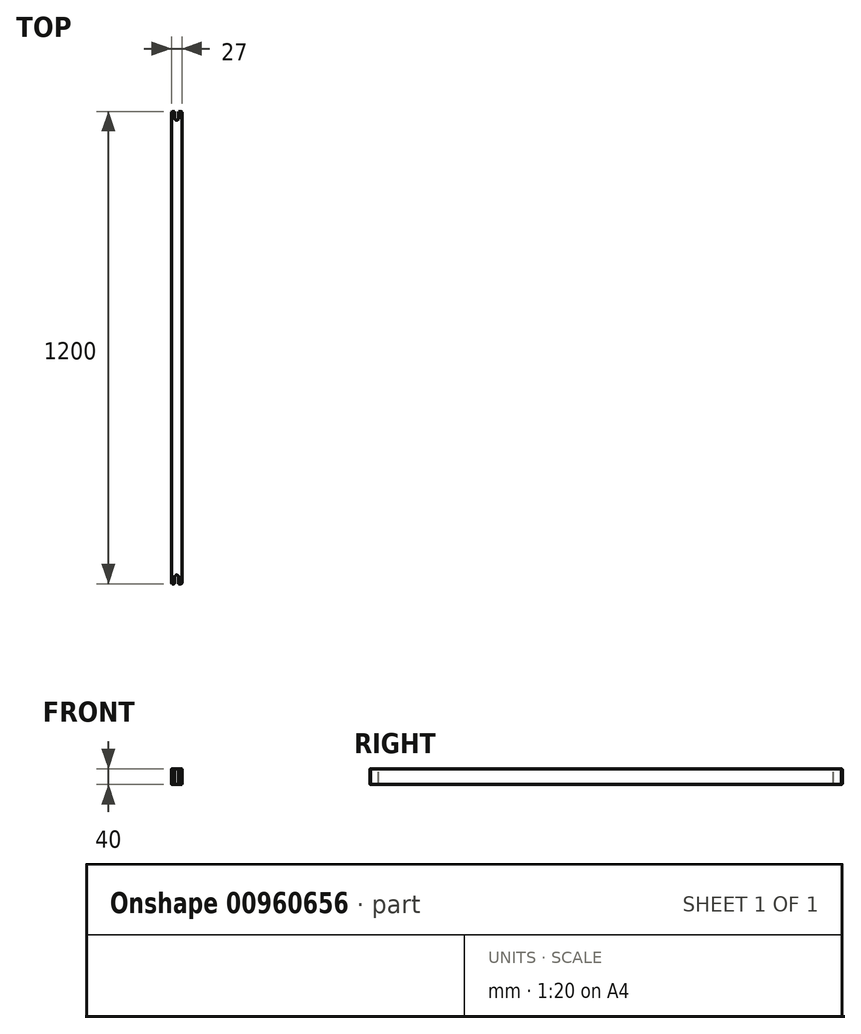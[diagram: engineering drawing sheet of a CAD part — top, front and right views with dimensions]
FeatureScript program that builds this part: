
annotation { "Feature Type Name" : "Feature", "Feature Type Description" : "" }
export const myFeature = defineFeature(function(context is Context, id is Id, definition is map)
    precondition{}
    {
        {
            var Q0;
            Q0=qCreatedBy(makeId("Front.planeOp"),FACE);
            var sketch = newSketch(context, id + "F0", { "sketchPlane" : qUnion([Q0])});
            skLineSegment(sketch, "E0.bottom", {"start": v(0, 0) * mm, "end": v(27, 0) * mm});
            skLineSegment(sketch, "E0.top", {"start": v(0, 40) * mm, "end": v(27, 40) * mm});
            skLineSegment(sketch, "E0.left", {"start": v(0, 0) * mm, "end": v(0, 40) * mm});
            skLineSegment(sketch, "E0.right", {"start": v(27, 0) * mm, "end": v(27, 40) * mm});
            skSolve(sketch);
        }
        {
            var Q0;
            Q0=makeQuery(id+"F0.imprint","IMPRINT",FACE,{"disambiguationData":[TD([[makeQuery(id+"F0.imprint","IMPRINT",EDGE,{"derivedFrom":sQuery(id+"F0.wireOp",EDGE,"E0.bottom")}),1.0]])]});
            extrude(context, id + "F1", {"entities" : qUnion([Q0]), "endBound" : BoundingType.SYMMETRIC, "depth" : 1200 * mm, "offsetDistance" : 25 * mm});
        }
        {
            var Q0;
            Q0=makeQuery(id+"F1.opExtrude","SWEPT_FACE",FACE,{"disambiguationData":[OSD([sQuery(id+"F0.wireOp",EDGE,"E0.top")])]});
            var sketch = newSketch(context, id + "F2", { "sketchPlane" : qUnion([Q0])});
            skArc(sketch, "E1", {"start": v(18.5, -583) * mm, "mid": v(13.5, -578) * mm, "end": v(8.5, -583) * mm});
            skPoint(sketch, "E1.centerSnap0", {"position": v(13.5, -600) * mm});
            skLineSegment(sketch, "E2.top", {"start": v(8.5, -600) * mm, "end": v(18.5, -600) * mm});
            skLineSegment(sketch, "E2.left", {"start": v(8.5, -583) * mm, "end": v(8.5, -600) * mm});
            skLineSegment(sketch, "E2.right", {"start": v(18.5, -583) * mm, "end": v(18.5, -600) * mm});
            skArc(sketch, "E3.MirrorCS", {"start": v(18.5, 583) * mm, "mid": v(13.5, 578) * mm, "end": v(8.5, 583) * mm});
            skLineSegment(sketch, "E4.MirrorCS", {"start": v(8.5, 600) * mm, "end": v(18.5, 600) * mm});
            skPoint(sketch, "E5.MirrorP", {"position": v(13.5, 600) * mm});
            skLineSegment(sketch, "E6.MirrorCS", {"start": v(18.5, 583) * mm, "end": v(18.5, 600) * mm});
            skLineSegment(sketch, "E7.MirrorCS", {"start": v(8.5, 583) * mm, "end": v(8.5, 600) * mm});
            skSolve(sketch);
        }
        {
            var Q0;
            Q0=makeQuery(id+"F2.imprint","IMPRINT",FACE,{"disambiguationData":[TD([[makeQuery(id+"F2.imprint","IMPRINT",EDGE,{"derivedFrom":sQuery(id+"F2.wireOp",EDGE,"E1")}),1.0]])]});
            extrude(context, id + "F3", {"entities" : qUnion([Q0]), "operationType" : NewBodyOperationType.REMOVE, "endBound" : BoundingType.THROUGH_ALL, "oppositeDirection" : true, "depth" : 25 * mm, "offsetDistance" : 25 * mm});
        }
        {
            var Q0;
            Q0 = qSketchRegion(id + "F2", true);
            extrude(context, id + "F4", {"entities" : qUnion([Q0]), "operationType" : NewBodyOperationType.REMOVE, "endBound" : BoundingType.THROUGH_ALL, "oppositeDirection" : true, "depth" : 25 * mm, "offsetDistance" : 25 * mm});
        }
        {
            var Q0;
            Q0=makeQuery(id+"F1.opExtrude","CAP_EDGE",EDGE,{"disambiguationData":[OSD([sQuery(id+"F0.wireOp",EDGE,"E0.left")])],"isStart":false});
            var Q1;
            Q1=makeQuery(id+"F1.opExtrude","CAP_EDGE",EDGE,{"disambiguationData":[OSD([sQuery(id+"F0.wireOp",EDGE,"E0.right")])],"isStart":false});
            var Q2;
            Q2=makeQuery(id+"F1.opExtrude","CAP_EDGE",EDGE,{"disambiguationData":[OSD([sQuery(id+"F0.wireOp",EDGE,"E0.left")])],"isStart":true});
            var Q3;
            Q3=makeQuery(id+"F1.opExtrude","CAP_EDGE",EDGE,{"disambiguationData":[OSD([sQuery(id+"F0.wireOp",EDGE,"E0.right")])],"isStart":true});
            chamfer(context, id + "F5", {"entities" : qUnion([Q0, Q1, Q2, Q3]), "width" : 2 * mm, "tangentPropagation" : true});
        }
        {
            var Q0;
            Q0=makeQuery(id+"F1.opExtrude","SWEPT_FACE",FACE,{"disambiguationData":[OSD([sQuery(id+"F0.wireOp",EDGE,"E0.top")])]});
            var Q1;
            Q1=makeQuery(id+"F1.opExtrude","SWEPT_FACE",FACE,{"disambiguationData":[OSD([sQuery(id+"F0.wireOp",EDGE,"E0.bottom")])]});
            var Q2;
            Q2=makeQuery(id+"F4.boolean.opBoolean","COPY",EDGE,{"derivedFrom":makeQuery(id+"F4.opExtrude","SWEPT_EDGE",EDGE,{"disambiguationData":[OSD([sQuery(id+"F0.wireOp",EDGE,"E0.top"),sQuery(id+"F2.wireOp",EDGE,"E4.MirrorCS"),sQuery(id+"F2.wireOp",EDGE,"E6.MirrorCS")])]})});
            var Q3;
            Q3=makeQuery(id+"F4.boolean.opBoolean","COPY",EDGE,{"derivedFrom":makeQuery(id+"F4.opExtrude","SWEPT_EDGE",EDGE,{"disambiguationData":[OSD([sQuery(id+"F0.wireOp",EDGE,"E0.top"),sQuery(id+"F2.wireOp",EDGE,"E4.MirrorCS"),sQuery(id+"F2.wireOp",EDGE,"E7.MirrorCS")])]})});
            var Q4;
            Q4=makeQuery(id+"F3.boolean.opBoolean","COPY",EDGE,{"derivedFrom":makeQuery(id+"F3.opExtrude","SWEPT_EDGE",EDGE,{"disambiguationData":[OSD([sQuery(id+"F0.wireOp",EDGE,"E0.top"),sQuery(id+"F2.wireOp",EDGE,"E2.top"),sQuery(id+"F2.wireOp",EDGE,"E2.right")])]})});
            var Q5;
            Q5=makeQuery(id+"F3.boolean.opBoolean","COPY",EDGE,{"derivedFrom":makeQuery(id+"F3.opExtrude","SWEPT_EDGE",EDGE,{"disambiguationData":[OSD([sQuery(id+"F0.wireOp",EDGE,"E0.top"),sQuery(id+"F2.wireOp",EDGE,"E2.top"),sQuery(id+"F2.wireOp",EDGE,"E2.left")])]})});
            fillet(context, id + "F6", {"entities" : qUnion([Q0, Q1, Q2, Q3, Q4, Q5]), "radius" : 2 * mm, "tangentPropagation" : true, "allowEdgeOverflow" : false});
        }
    });
